# Revit family: Bath-Walk-In-KOHLER-Belay-K-23768T_1
name_source: partatom
category: Plumbing Fixtures
units: mm (PartAtom-declared; Revit-internal decimal feet)

## family parameters
Cut with Voids When Loaded = No
Host = Face
Maintain Annotation Orientation = No
OmniClass Number = 23.31.15.00
OmniClass Title = Bathtubs
Part Type = Normal
Room Calculation Point = No
Round Connector Dimension = Use Diameter
Shared = No

## types (2) — shared parameters
ADA Compliant = No
Assembly Code = D2010500
CW Connection = No
Cold Water Inlet = Cold Water Inlet
Date Modified = 02/19/2023
Default Elevation = 0"
Drain Included = No
Finish = KOHLER-Acrylic-0-White
Flow Rate = 0 GPM
HW Connection = No
Height = 41 7/8"
Hot Water Inlet = Hot Water Inlet
Length = 60"
Manufacturer = Kohler Co.
Master Format 2014 = 22 41 19
Master Format 2014 Name = Residential Bathtubs
Material = Acrylic
Pressure = 0.00 psi
Product Documentation Link = https://files.kohler.com.cn
Product Name = Belay
Product Page URL = https://www.kohler.com.cn
URL = http://www.kohler.com.cn
Vent Connection = No
Waste Connection = Yes
Waste Water Outlet = Waste Water Outlet
WaterSense Certified = No
Width = 32"

## per-type parameters (varying)
| type | Description | Distance Of Connector | Left Drain | Model | Right Drain | Type |
| Left Drain, 0-White | Belling walk-in bathtub (left door 150mm version) | 41 15/16" | Yes | K-23768T-LCP-0 | No | 1 |
| Right Drain, 0-White | Baying walk-in bathtub (right door 150mm version)) | 18" | No | K-23768T-RCP-0 | Yes | 2 |

## geometry (parser evidence)
native form markers: Sweep x5
no freeform markers — native parametric forms only
